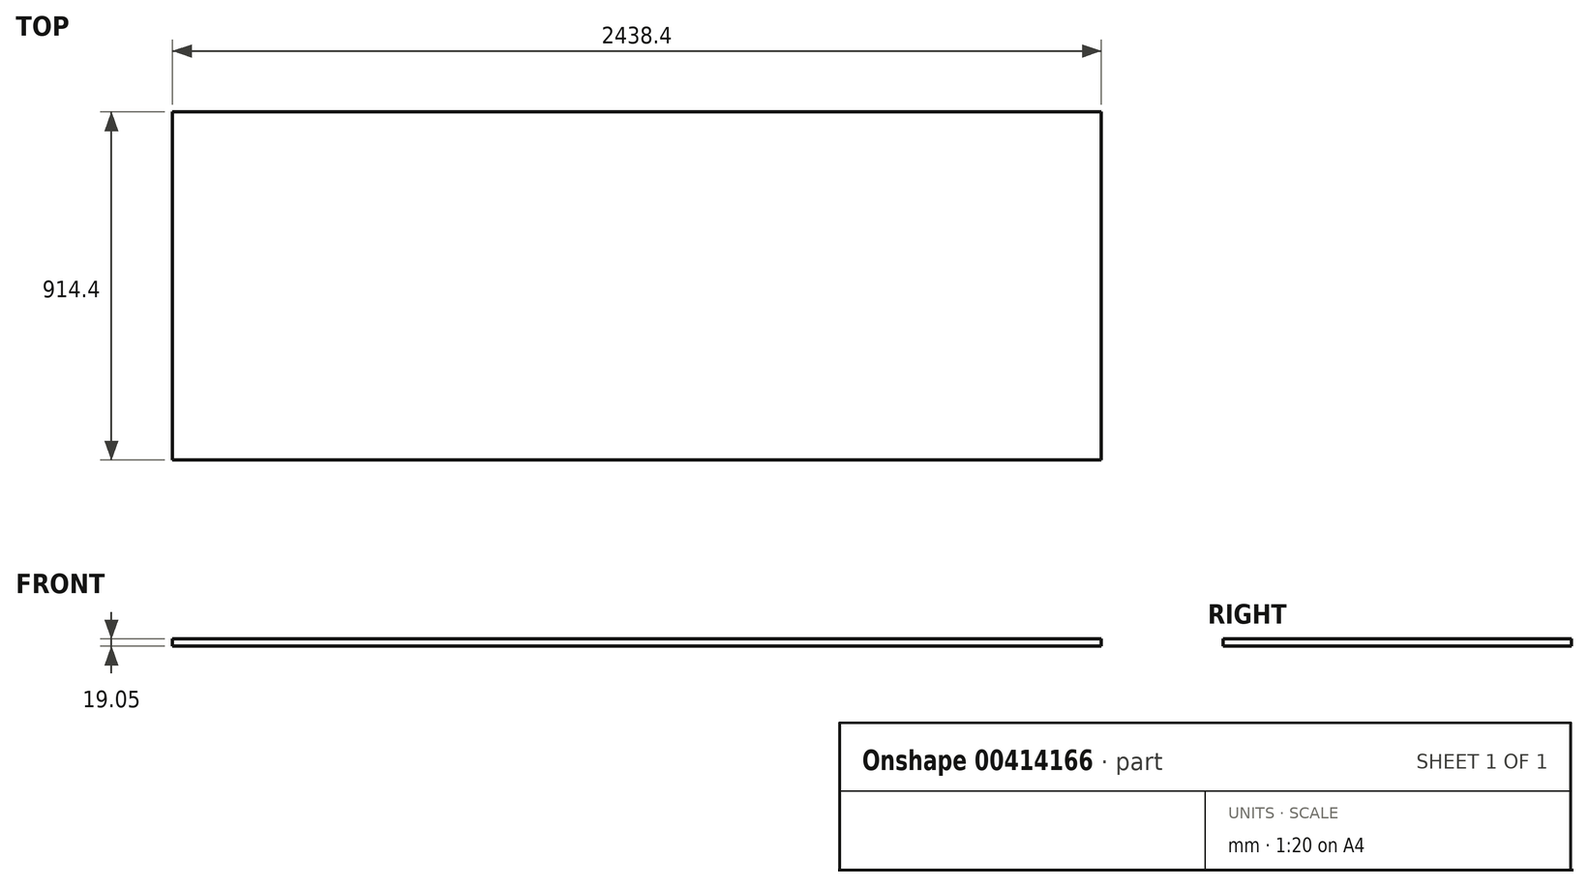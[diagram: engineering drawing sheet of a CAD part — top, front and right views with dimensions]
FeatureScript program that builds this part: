
annotation { "Feature Type Name" : "Feature", "Feature Type Description" : "" }
export const myFeature = defineFeature(function(context is Context, id is Id, definition is map)
    precondition{}
    {
        {
            var Q0;
            Q0=qCreatedBy(makeId("Top.planeOp"),FACE);
            var sketch = newSketch(context, id + "F0", { "sketchPlane" : qUnion([Q0])});
            skLineSegment(sketch, "E0.bottom", {"start": v(-1219.2, 457.2) * mm, "end": v(1219.2, 457.2) * mm});
            skLineSegment(sketch, "E0.top", {"start": v(-1219.2, -457.2) * mm, "end": v(1219.2, -457.2) * mm});
            skLineSegment(sketch, "E0.left", {"start": v(-1219.2, 457.2) * mm, "end": v(-1219.2, -457.2) * mm});
            skLineSegment(sketch, "E0.right", {"start": v(1219.2, 457.2) * mm, "end": v(1219.2, -457.2) * mm});
            skSolve(sketch);
        }
        {
            var Q0;
            Q0 = qSketchRegion(id + "F0", true);
            extrude(context, id + "F1", {"entities" : qUnion([Q0]), "depth" : 19.05 * mm});
        }
    });
